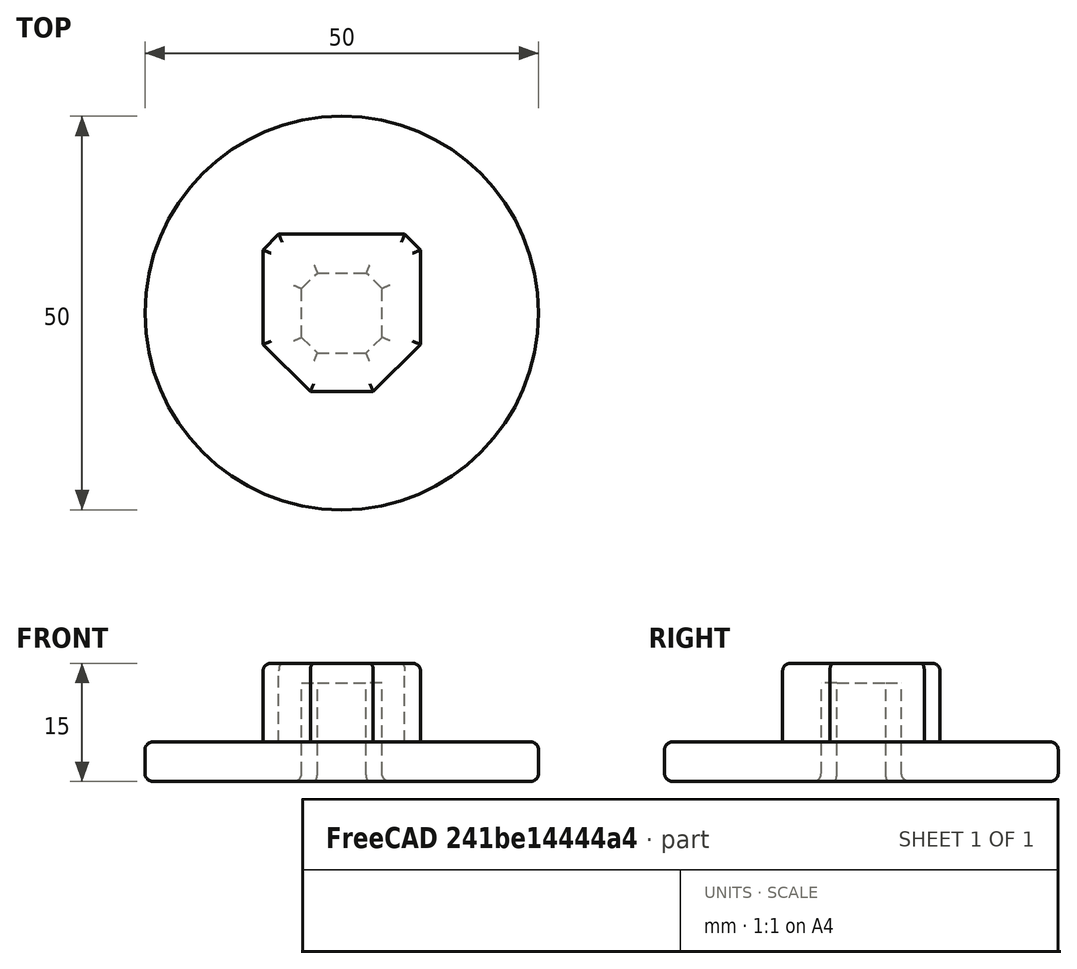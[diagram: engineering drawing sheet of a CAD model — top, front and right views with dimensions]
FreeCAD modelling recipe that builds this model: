
FCSTD DOCUMENT  (FreeCAD 0.14R3703 (Git))
Label: GOUM_Roller-Side1
License: CC-BY 3.0
LicenseURL: http://creativecommons.org/licenses/by/3.0/
objects: Part::Chamfer×3, Part::Fillet×3, Part::Box×2, Part::Cylinder×1, Part::MultiFuse×1, Part::Cut×1
note: 11 computed .brp shape members not serialized (recipe doc carries the construction recipe); baked Part::Feature solids carry a one-line shape summary decoded from their .brp

FEATURE [Part::Box] Box  label="Cube"
  Height = 10
  Length = 20
  Placement = pos=(-10,-10,5) rot=(0,0,1;0rad)
  Width = 20
FEATURE [Part::Chamfer] Chamfer
  Base = -> Box
  Edges = 2 edges r=6: [Edge1,Edge5]
FEATURE [Part::Chamfer] Chamfer001
  Base = -> Chamfer
  Edges = 2 edges r=2: [Edge3,Edge13]
FEATURE [Part::Box] Box001  label="Cube001"
  Height = 12.5
  Length = 10.2
  Placement = pos=(-5.1,-5.1,0) rot=(0,0,1;0rad)
  Width = 10.2
FEATURE [Part::Cylinder] Cylinder
  Angle = 360
  Height = 5
  Radius = 25
FEATURE [Part::Chamfer] Chamfer002  label="Chamfered hole"
  Base = -> Box001
  Edges = 4 edges r=2: [Edge1,Edge3,Edge5,Edge7]
FEATURE [Part::Fillet] Fillet  label="Side"
  Base = -> Cylinder
  Edges = 2 edges r=1: [Edge1,Edge3]
FEATURE [Part::Fillet] Fillet001
  Base = -> Chamfer001
  Edges = 8 edges r=1: [Edge1,Edge5,Edge6,Edge7,Edge8,Edge9,Edge10,Edge11]
FEATURE [Part::MultiFuse] Fusion
  Shapes = -> [Fillet,Fillet001]
FEATURE [Part::Cut] Cut
  Base = -> Fusion
  Tool = -> Chamfer002
FEATURE [Part::Fillet] Fillet002  label="PRINT2_Side-with-support"
  Base = -> Cut
  Edges = 8 edges r=1: [Edge8,Edge9,Edge10,Edge11,Edge12,Edge13,Edge14,Edge15]
